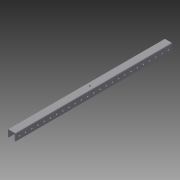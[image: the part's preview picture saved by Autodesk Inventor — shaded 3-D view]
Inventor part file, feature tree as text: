
AUTODESK INVENTOR PART (.ipt)
format: ipt  version: 2015 (Build 190159000, 159)  size: 435,200 bytes
history: native  units: in
note: dims shown in document units (in); Inventor stores cm internally (conversion verified against a paired STEP export)
features: extrude x3, sketch x3, pattern_linear x1
ambient origin geometry x8: Origin, YZ Plane, XZ Plane, XY Plane, X Axis, Y Axis, Z Axis, Center Point
bodies: Solid1 (feature_tree)
feature tree (7):
  extrude  "Extrusion1"  Depth=25.26in
  extrude  "Extrusion4"  Depth=0.5in
  pattern_linear  "Rectangular Pattern3"  Spacing1=0.25in  [1 undecoded]
  extrude  "Extrusion5"  Depth=1.0in TaperAngle=0.0deg
  sketch  "Sketch1"  dims[d0=1.13in d1=1.25in d2=0.125in d3=0.125in d4=0.125in d5=25.26in]
  sketch  "Sketch4"  dims[d6=0.0in d34=0.5in]
  sketch  "Sketch5"  dims[d35=0.0in d36=0.25in d37=1.0in d38=0.0in d39=11.811in d41=1.0in d42=11.811in d44=1.0in d45=0.25in d46=1.0in d47=0.0in]
note: 1 required parameter value undecoded (feature->parameter linkage not recoverable at this tier; creation-order binding heuristic only, values carry confidence <= 0.55)
